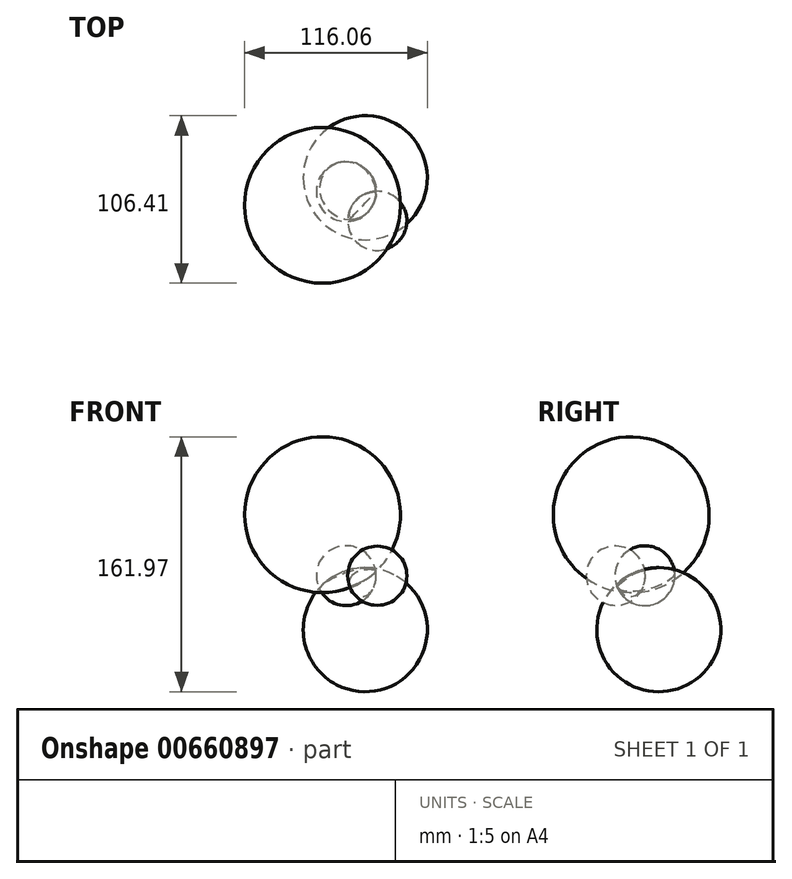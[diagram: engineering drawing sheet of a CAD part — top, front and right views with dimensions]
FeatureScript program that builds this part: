
annotation { "Feature Type Name" : "Feature", "Feature Type Description" : "" }
export const myFeature = defineFeature(function(context is Context, id is Id, definition is map)
    precondition{}
    {
        {
            var Q0;
            Q0=qCreatedBy(makeId("Top.planeOp"),FACE);
            var sketch = newSketch(context, id + "F0", { "sketchPlane" : qUnion([Q0])});
            skArc(sketch, "E0", {"start": v(-42.18, 9.94) * mm, "mid": v(-57.73, -12) * mm, "end": v(-35.8, -27.55) * mm});
            skLineSegment(sketch, "E1", {"start": v(-35.8, -27.55) * mm, "end": v(-42.18, 9.94) * mm});
            skSolve(sketch);
        }
        {
            var Q0;
            Q0=makeQuery(id+"F0.imprint","IMPRINT",FACE,{"disambiguationData":[TD([[makeQuery(id+"F0.imprint","IMPRINT",EDGE,{"derivedFrom":sQuery(id+"F0.wireOp",EDGE,"E0")}),1.0]])]});
            var Q1;
            Q1=sQuery(id+"F0.wireOp",EDGE,"E1");
            revolve(context, id + "F1", {"surfaceOperationType" : NewSurfaceOperationType.NEW, "entities" : qUnion([Q0]), "axis" : qUnion([Q1]), "revolveType" : RevolveType.FULL});
        }
        {
            var Q0;
            Q0=qCreatedBy(makeId("Top.planeOp"),FACE);
            var sketch = newSketch(context, id + "F2", { "sketchPlane" : qUnion([Q0])});
            skArc(sketch, "E2", {"start": v(-6.23, -13.8) * mm, "mid": v(-32.8, -14.3) * mm, "end": v(-32.3, -40.87) * mm});
            skLineSegment(sketch, "E3", {"start": v(-32.3, -40.87) * mm, "end": v(-19.26, -27.33) * mm});
            skLineSegment(sketch, "E4", {"start": v(-19.26, -27.33) * mm, "end": v(-6.23, -13.8) * mm});
            skSolve(sketch);
        }
        {
            var Q0;
            Q0=makeQuery(id+"F2.imprint","IMPRINT",FACE,{"disambiguationData":[TD([[makeQuery(id+"F2.imprint","IMPRINT",EDGE,{"derivedFrom":sQuery(id+"F2.wireOp",EDGE,"E2")}),1.0]])]});
            var Q1;
            Q1=sQuery(id+"F2.wireOp",EDGE,"E3");
            revolve(context, id + "F3", {"surfaceOperationType" : NewSurfaceOperationType.NEW, "entities" : qUnion([Q0]), "axis" : qUnion([Q1]), "revolveType" : RevolveType.FULL});
        }
        {
            var Q0;
            Q0=qCreatedBy(makeId("Front.planeOp"),FACE);
            var sketch = newSketch(context, id + "F4", { "sketchPlane" : qUnion([Q0])});
            skArc(sketch, "E5", {"start": v(-8.65, 0.64) * mm, "mid": v(-61.82, -16.06) * mm, "end": v(-45.1, -69.24) * mm});
            skLineSegment(sketch, "E6", {"start": v(-26.88, -34.3) * mm, "end": v(-45.1, -69.24) * mm});
            skLineSegment(sketch, "E7", {"start": v(-26.88, -34.3) * mm, "end": v(-8.65, 0.64) * mm});
            skSolve(sketch);
        }
        {
            var Q0;
            Q0=makeQuery(id+"F4.imprint","IMPRINT",FACE,{"disambiguationData":[TD([[makeQuery(id+"F4.imprint","IMPRINT",EDGE,{"derivedFrom":sQuery(id+"F4.wireOp",EDGE,"E5")}),1.0]])]});
            var Q1;
            Q1=sQuery(id+"F4.wireOp",EDGE,"E7");
            revolve(context, id + "F5", {"surfaceOperationType" : NewSurfaceOperationType.NEW, "entities" : qUnion([Q0]), "axis" : qUnion([Q1]), "revolveType" : RevolveType.FULL});
        }
        {
            var Q0;
            Q0=makeQuery(id+"F5.opRevolve","SWEPT_BODY",BODY,{"disambiguationData":[OSD([sQuery(id+"F4.wireOp",EDGE,"E5"),sQuery(id+"F4.wireOp",EDGE,"E6"),sQuery(id+"F4.wireOp",EDGE,"E7")])]});
            var Q1;
            Q1=makeQuery(id+"F1.opRevolve","SWEPT_BODY",BODY,{"disambiguationData":[OSD([sQuery(id+"F0.wireOp",EDGE,"E0"),sQuery(id+"F0.wireOp",EDGE,"E1")])]});
            booleanBodies(context, id + "F6", {"operationType" : BooleanOperationType.INTERSECTION, "tools" : qUnion([Q0, Q1]), "keepTools" : true});
        }
        {
            var Q0;
            Q0=makeQuery(id+"F6.opBoolean","INTERSECT",BODY,{"derivedFrom":[makeQuery(id+"F1.opRevolve","SWEPT_BODY",BODY,{"disambiguationData":[OSD([sQuery(id+"F0.wireOp",EDGE,"E0"),sQuery(id+"F0.wireOp",EDGE,"E1")])]}),makeQuery(id+"F5.opRevolve","SWEPT_BODY",BODY,{"disambiguationData":[OSD([sQuery(id+"F4.wireOp",EDGE,"E5"),sQuery(id+"F4.wireOp",EDGE,"E6"),sQuery(id+"F4.wireOp",EDGE,"E7")])]})]});
            var Q1;
            Q1=makeQuery(id+"F3.opRevolve","SWEPT_BODY",BODY,{"disambiguationData":[OSD([sQuery(id+"F2.wireOp",EDGE,"E2"),sQuery(id+"F2.wireOp",EDGE,"E3"),sQuery(id+"F2.wireOp",EDGE,"E4")])]});
            booleanBodies(context, id + "F7", {"operationType" : BooleanOperationType.INTERSECTION, "tools" : qUnion([Q0, Q1]), "keepTools" : true});
        }
        {
            var Q0;
            Q0=makeQuery(id+"F7.opBoolean","INTERSECT",VERTEX,{"disambiguationData":[OD(0.0)],"derivedFrom":[makeQuery(id+"F3.opRevolve","SWEPT_FACE",FACE,{"disambiguationData":[OSD([sQuery(id+"F2.wireOp",EDGE,"E2")])]}),makeQuery(id+"F6.opBoolean","COPY",FACE,{"derivedFrom":makeQuery(id+"F1.opRevolve","SWEPT_FACE",FACE,{"disambiguationData":[OSD([sQuery(id+"F0.wireOp",EDGE,"E0")])]})}),makeQuery(id+"F6.opBoolean","COPY",FACE,{"derivedFrom":makeQuery(id+"F5.opRevolve","SWEPT_FACE",FACE,{"disambiguationData":[OSD([sQuery(id+"F4.wireOp",EDGE,"E5")])]})})]});
            var Q1;
            Q1=makeQuery(id+"F7.opBoolean","INTERSECT",VERTEX,{"disambiguationData":[OD(1.0)],"derivedFrom":[makeQuery(id+"F3.opRevolve","SWEPT_FACE",FACE,{"disambiguationData":[OSD([sQuery(id+"F2.wireOp",EDGE,"E2")])]}),makeQuery(id+"F6.opBoolean","COPY",FACE,{"derivedFrom":makeQuery(id+"F1.opRevolve","SWEPT_FACE",FACE,{"disambiguationData":[OSD([sQuery(id+"F0.wireOp",EDGE,"E0")])]})}),makeQuery(id+"F6.opBoolean","COPY",FACE,{"derivedFrom":makeQuery(id+"F5.opRevolve","SWEPT_FACE",FACE,{"disambiguationData":[OSD([sQuery(id+"F4.wireOp",EDGE,"E5")])]})})]});
            cPlane(context, id + "F8", {"entities" : qUnion([Q0, Q1]), "cplaneType" : CPlaneType.MID_PLANE, "offset" : 25.4 * mm, "width" : 152.4 * mm, "height" : 152.4 * mm});
        }
        {
            var Q0;
            Q0=qCreatedBy(id+"F8.planeOp",FACE);
            var sketch = newSketch(context, id + "F9", { "sketchPlane" : qUnion([Q0])});
            skArc(sketch, "E8", {"start": v(-4.34, 47.63) * mm, "mid": v(39.52, -6.94) * mm, "end": v(94.08, 36.92) * mm});
            skLineSegment(sketch, "E9", {"start": v(44.87, 42.27) * mm, "end": v(-4.34, 47.63) * mm});
            skLineSegment(sketch, "E10", {"start": v(44.87, 42.27) * mm, "end": v(94.08, 36.92) * mm});
            skSolve(sketch);
        }
        {
            var Q0;
            Q0=makeQuery(id+"F9.imprint","IMPRINT",FACE,{"disambiguationData":[TD([[makeQuery(id+"F9.imprint","IMPRINT",EDGE,{"derivedFrom":sQuery(id+"F9.wireOp",EDGE,"E8")}),1.0]])]});
            var Q1;
            Q1=sQuery(id+"F9.wireOp",EDGE,"E9");
            revolve(context, id + "F10", {"surfaceOperationType" : NewSurfaceOperationType.NEW, "entities" : qUnion([Q0]), "axis" : qUnion([Q1]), "revolveType" : RevolveType.FULL});
        }
    });
